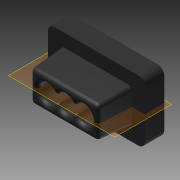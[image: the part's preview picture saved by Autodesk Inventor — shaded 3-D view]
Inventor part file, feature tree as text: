
AUTODESK INVENTOR PART (.ipt)
format: ipt  version: 2013 (Build 170138000, 138)  size: 184,832 bytes
history: native  units: in
note: dims shown in document units (in); Inventor stores cm internally (conversion verified against a paired STEP export)
features: extrude x3, sketch x3, fillet x2, plane x1
ambient origin geometry x8: Origin, YZ Plane, XZ Plane, XY Plane, X Axis, Y Axis, Z Axis, Center Point
bodies: Solid1 (feature_tree)
feature tree (9):
  extrude  "Extrusion1"  Depth=0.185in
  extrude  "Extrusion2"  Depth=0.217in
  fillet  "Fillet1"  Radius=0.106in
  extrude  "Extrusion3"  Depth=0.02in
  fillet  "Fillet2"  Radius=0.098in
  plane  "Work Plane1"
  sketch  "Sketch1"  dims[d0=0.295in d1=0.185in]
  sketch  "Sketch2"  dims[d2=0.059in d3=0.0in d4=0.217in d5=0.106in]
  sketch  "Sketch3"  dims[d6=0.098in d7=-0.0236in d8=0.02in d9=0.098in d10=0.0in d11=0.012in]
